# Revit family: raspashnie_protivopozarnie_vorota_firetechnics-d_ei60
name_source: partatom
category: Двери
revit_build: Autodesk Revit 2018 (Build: 20170223_1515(x64)
units: mm (PartAtom-declared; Revit-internal decimal feet)

## family parameters
Всегда вертикально = Да
Заголовок OmniClass = Doors
Номер OmniClass = 23.30.10.00
Общий = Нет
Основа = Стена
При загрузке вырезать с полостями = Нет
Точка расчета площади = Нет

## types (1)
- Распашные противопажарные ворота FireTechnics-D EI60
    ADSK_URL страницы изделия = https://www.fire-tec.ru
    ADSK_Наименование = Распашные противопажарные ворота Firetechnics-D EI60
    ADSK_Предел огнестойкости = EI60
    ADSK_Размер_Высота = 3000 мм
    ADSK_Размер_Ширина = 4000 мм
    URL = https://www.fire-tec.ru
    Аналитическая конструкция = <Нет>
    Высота = 3000 мм
    Высота поперечного бруса = 120 мм
    Высота противопожарной двери = 2000 мм
    Замыкание стены = По основе
    Изготовитель = Firetechnics
    Материал полотна = Полотно с наполнителем из минерального заполнителя
    Материал ручки = СВМПЭ, черный
    Материал стоек = Сталь_оцинкованная_листовая Firetechnics
    Огнестойкость = EI60
    Резервирование простанства = Границы резервирования пространства
    Функция = Внутренние слои
    Ширина = 4000 мм
    Ширина двери = 1100 мм
    Ширина стоек = 70 мм
    Ширина стойки = 54 мм
    ширина полотна = 90 мм

## geometry (parser evidence)
native form markers: Blend x2
no freeform markers — native parametric forms only
